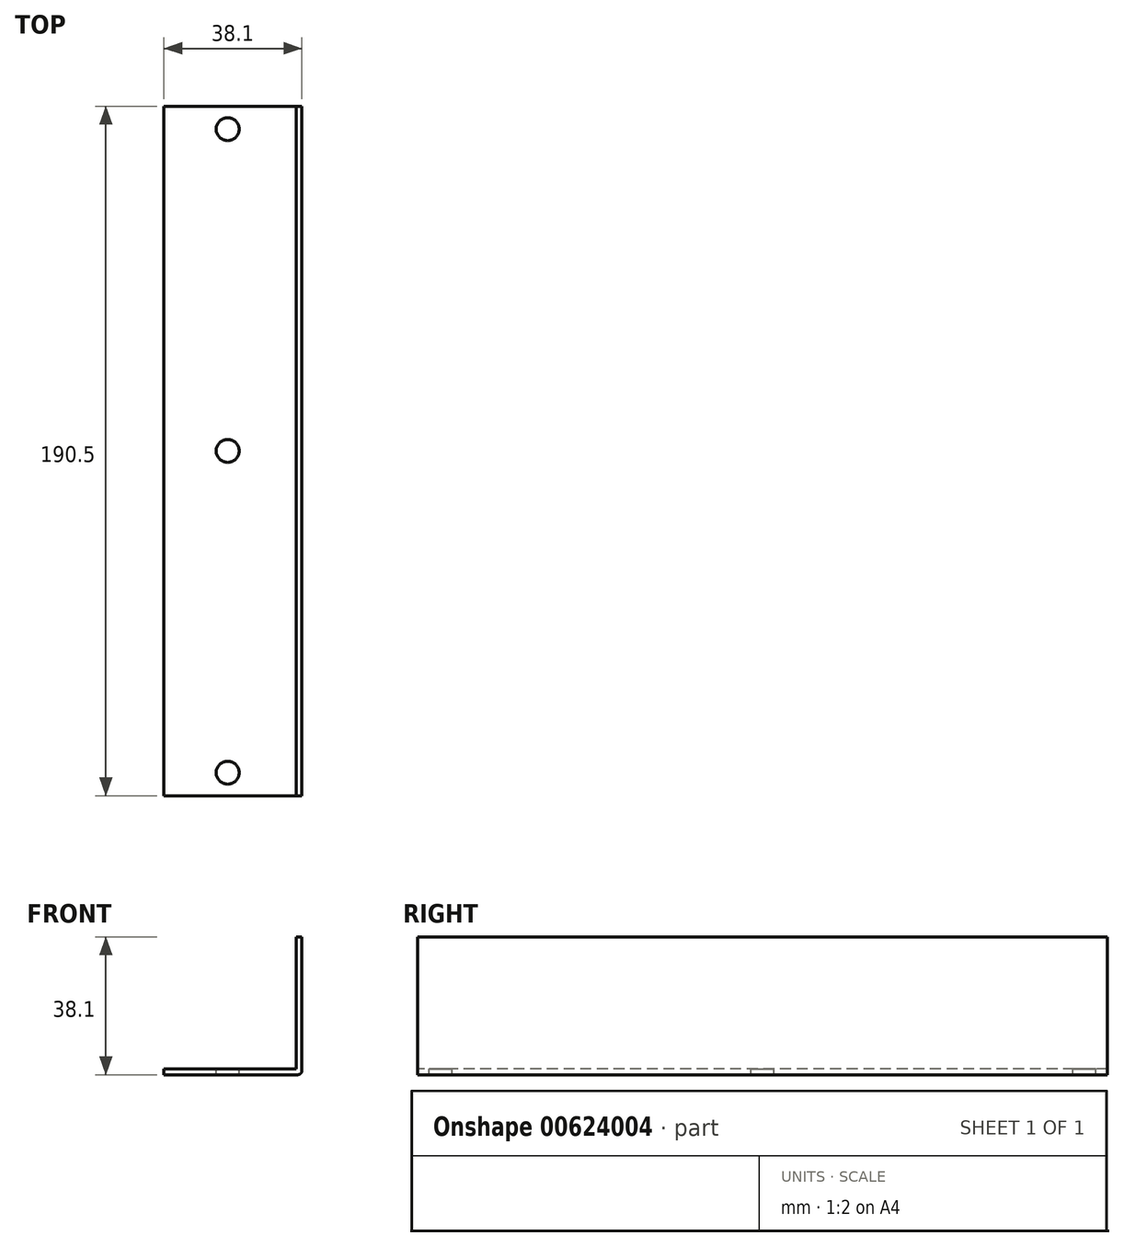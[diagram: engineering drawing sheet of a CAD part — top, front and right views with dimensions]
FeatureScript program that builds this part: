
annotation { "Feature Type Name" : "Feature", "Feature Type Description" : "" }
export const myFeature = defineFeature(function(context is Context, id is Id, definition is map)
    precondition{}
    {
        {
            var Q0;
            Q0=qCreatedBy(makeId("Top.planeOp"),FACE);
            var sketch = newSketch(context, id + "F0", { "sketchPlane" : qUnion([Q0])});
            skLineSegment(sketch, "E0.bottom", {"start": v(-53.6, 131.73) * mm, "end": v(-15.5, 131.73) * mm});
            skLineSegment(sketch, "E0.top", {"start": v(-53.6, -58.77) * mm, "end": v(-15.5, -58.77) * mm});
            skLineSegment(sketch, "E0.left", {"start": v(-53.6, 131.73) * mm, "end": v(-53.6, -58.77) * mm});
            skLineSegment(sketch, "E0.right", {"start": v(-15.5, 131.73) * mm, "end": v(-15.5, -58.77) * mm});
            skSolve(sketch);
        }
        {
            var Q0;
            Q0=makeQuery(id+"F0.imprint","IMPRINT",FACE,{"disambiguationData":[TD([[makeQuery(id+"F0.imprint","IMPRINT",EDGE,{"derivedFrom":sQuery(id+"F0.wireOp",EDGE,"E0.bottom")}),-1.0]])]});
            extrude(context, id + "F1", {"entities" : qUnion([Q0]), "depth" : 1.59 * mm, "offsetDistance" : 25.4 * mm});
        }
        {
            var Q0;
            Q0=makeQuery(id+"F1.opExtrude","CAP_FACE",FACE,{"disambiguationData":[OSD([sQuery(id+"F0.wireOp",EDGE,"E0.bottom"),sQuery(id+"F0.wireOp",EDGE,"E0.top"),sQuery(id+"F0.wireOp",EDGE,"E0.left"),sQuery(id+"F0.wireOp",EDGE,"E0.right")])],"isStart":false});
            var sketch = newSketch(context, id + "F2", { "sketchPlane" : qUnion([Q0])});
            skLineSegment(sketch, "E1.bottom", {"start": v(-15.5, 131.73) * mm, "end": v(-17.09, 131.73) * mm});
            skLineSegment(sketch, "E1.top", {"start": v(-15.5, -58.77) * mm, "end": v(-17.09, -58.77) * mm});
            skLineSegment(sketch, "E1.left", {"start": v(-15.5, 131.73) * mm, "end": v(-15.5, -58.77) * mm});
            skLineSegment(sketch, "E1.right", {"start": v(-17.09, 131.73) * mm, "end": v(-17.09, -58.77) * mm});
            skSolve(sketch);
        }
        {
            var Q0;
            Q0=makeQuery(id+"F2.imprint","IMPRINT",FACE,{"disambiguationData":[TD([[makeQuery(id+"F2.imprint","IMPRINT",EDGE,{"derivedFrom":sQuery(id+"F2.wireOp",EDGE,"E1.bottom")}),-1.0]])]});
            extrude(context, id + "F3", {"entities" : qUnion([Q0]), "operationType" : NewBodyOperationType.ADD, "depth" : 36.5 * mm, "offsetDistance" : 25.4 * mm});
        }
        {
            var Q0;
            Q0=makeQuery(id+"F3.opExtrude","CAP_EDGE",EDGE,{"disambiguationData":[OSD([sQuery(id+"F2.wireOp",EDGE,"E1.right")])],"isStart":true});
            var Q1;
            Q1=makeQuery(id+"F1.opExtrude","CAP_EDGE",EDGE,{"disambiguationData":[OSD([sQuery(id+"F0.wireOp",EDGE,"E0.right")])],"isStart":true});
            fillet(context, id + "F4", {"entities" : qUnion([Q0, Q1]), "radius" : 1.27 * mm, "tangentPropagation" : true, "rho" : 0.5, "crossSection" : FilletCrossSection.CONIC, "allowEdgeOverflow" : false});
        }
        {
            var Q0;
            Q0=makeQuery(id+"F1.opExtrude","CAP_FACE",FACE,{"disambiguationData":[OSD([sQuery(id+"F0.wireOp",EDGE,"E0.bottom"),sQuery(id+"F0.wireOp",EDGE,"E0.top"),sQuery(id+"F0.wireOp",EDGE,"E0.left"),sQuery(id+"F0.wireOp",EDGE,"E0.right")])],"isStart":false});
            var sketch = newSketch(context, id + "F5", { "sketchPlane" : qUnion([Q0])});
            skCircle(sketch, "E2", {"center": v(-35.98, 36.48) * mm, "radius": 3.18 * mm});
            skPoint(sketch, "E2.centerSnap0", {"position": v(-53.6, 36.48) * mm});
            skPoint(sketch, "E2.centerSnap1", {"position": v(-35.98, 131.73) * mm});
            skSolve(sketch);
        }
        {
            var Q0;
            Q0=makeQuery(id+"F5.imprint","IMPRINT",FACE,{"disambiguationData":[TD([[makeQuery(id+"F5.imprint","IMPRINT",EDGE,{"derivedFrom":sQuery(id+"F5.wireOp",EDGE,"E2")}),1.0]])]});
            extrude(context, id + "F6", {"entities" : qUnion([Q0]), "operationType" : NewBodyOperationType.REMOVE, "oppositeDirection" : true, "depth" : 1.59 * mm, "offsetDistance" : 25.4 * mm});
        }
        {
            var Q0;
            Q0=makeQuery(id+"F1.opExtrude","CAP_FACE",FACE,{"disambiguationData":[OSD([sQuery(id+"F0.wireOp",EDGE,"E0.bottom"),sQuery(id+"F0.wireOp",EDGE,"E0.top"),sQuery(id+"F0.wireOp",EDGE,"E0.left"),sQuery(id+"F0.wireOp",EDGE,"E0.right")])],"isStart":false});
            var sketch = newSketch(context, id + "F7", { "sketchPlane" : qUnion([Q0])});
            skCircle(sketch, "E3", {"center": v(-35.98, 125.38) * mm, "radius": 3.18 * mm});
            skPoint(sketch, "E3.centerSnap0", {"position": v(-35.98, 131.73) * mm});
            skCircle(sketch, "E4", {"center": v(-35.98, -52.42) * mm, "radius": 3.18 * mm});
            skPoint(sketch, "E4.centerSnap0", {"position": v(-35.98, -58.77) * mm});
            skSolve(sketch);
        }
        {
            var Q0;
            Q0=makeQuery(id+"F7.imprint","IMPRINT",FACE,{"disambiguationData":[TD([[makeQuery(id+"F7.imprint","IMPRINT",EDGE,{"derivedFrom":sQuery(id+"F7.wireOp",EDGE,"E4")}),1.0]])]});
            var Q1;
            Q1=makeQuery(id+"F7.imprint","IMPRINT",FACE,{"disambiguationData":[TD([[makeQuery(id+"F7.imprint","IMPRINT",EDGE,{"derivedFrom":sQuery(id+"F7.wireOp",EDGE,"E3")}),1.0]])]});
            extrude(context, id + "F8", {"entities" : qUnion([Q0, Q1]), "operationType" : NewBodyOperationType.REMOVE, "oppositeDirection" : true, "depth" : 1.59 * mm, "offsetDistance" : 25.4 * mm});
        }
    });
